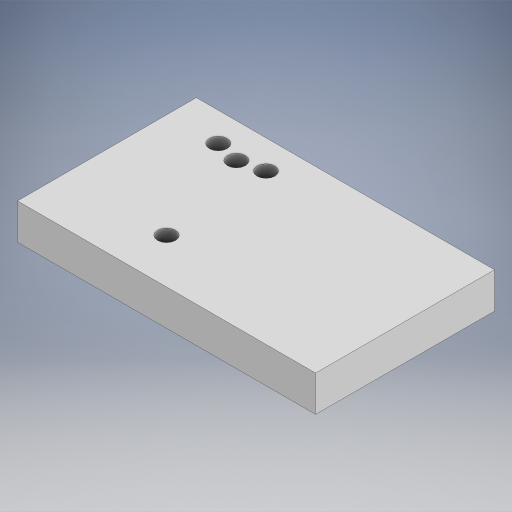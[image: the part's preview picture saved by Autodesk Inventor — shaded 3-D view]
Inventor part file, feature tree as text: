
AUTODESK INVENTOR PART (.ipt)
format: ipt  version: 2024 (Build 280153000, 153)  size: 231,936 bytes
history: native  units: mm
features: sketch x4, hole x3, extrude x1
ambient origin geometry x8: Origin, YZ Plane, XZ Plane, XY Plane, X Axis, Y Axis, Z Axis, Center Point
bodies: Volumenkörper1 (feature_tree)
feature tree (8):
  extrude  "Extrusion1"  Depth=60.0mm
  hole  "Bohrung1"  [1 undecoded]
  hole  "Bohrung3"  [1 undecoded]
  hole  "Bohrung5"  [1 undecoded]
  sketch  "Skizze1"  dims[d0=100.0mm d1=60.0mm]
  sketch  "Skizze2"  dims[d2=12.0mm d3=0.0mm]
  sketch  "Skizze4"  dims[d4=6.0mm d5=6.0mm d6=4.0mm d7=2.0mm d8=90.0deg d9=8.0mm d10=20.594885mm]
  sketch  "Skizze6"  dims[d18=6.0mm d19=6.0mm d20=4.0mm d21=2.0mm d22=90.0deg d23=8.0mm d24=20.594885mm d32=6.0mm d33=6.0mm d34=4.0mm d35=2.0mm d36=90.0deg d37=8.0mm d38=20.594885mm]
note: 3 required parameter values undecoded (feature->parameter linkage not recoverable at this tier; creation-order binding heuristic only, values carry confidence <= 0.55)
